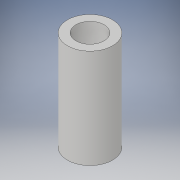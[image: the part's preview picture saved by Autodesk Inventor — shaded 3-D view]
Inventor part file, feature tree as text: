
AUTODESK INVENTOR PART (.ipt)
format: ipt  version: 2018 (Build 220112000, 112)  size: 94,720 bytes
history: native  units: in
note: dims shown in document units (in); Inventor stores cm internally (conversion verified against a paired STEP export)
features: extrude x1, sketch x1
ambient origin geometry x8: Origin, YZ Plane, XZ Plane, XY Plane, X Axis, Y Axis, Z Axis, Center Point
bodies: Solid1 (feature_tree)
feature tree (2):
  extrude  "Extrusion1"  Depth=1.1in
  sketch  "Sketch1"  dims[d0=0.5in d1=0.312in d2=1.1in d3=0.0in]
